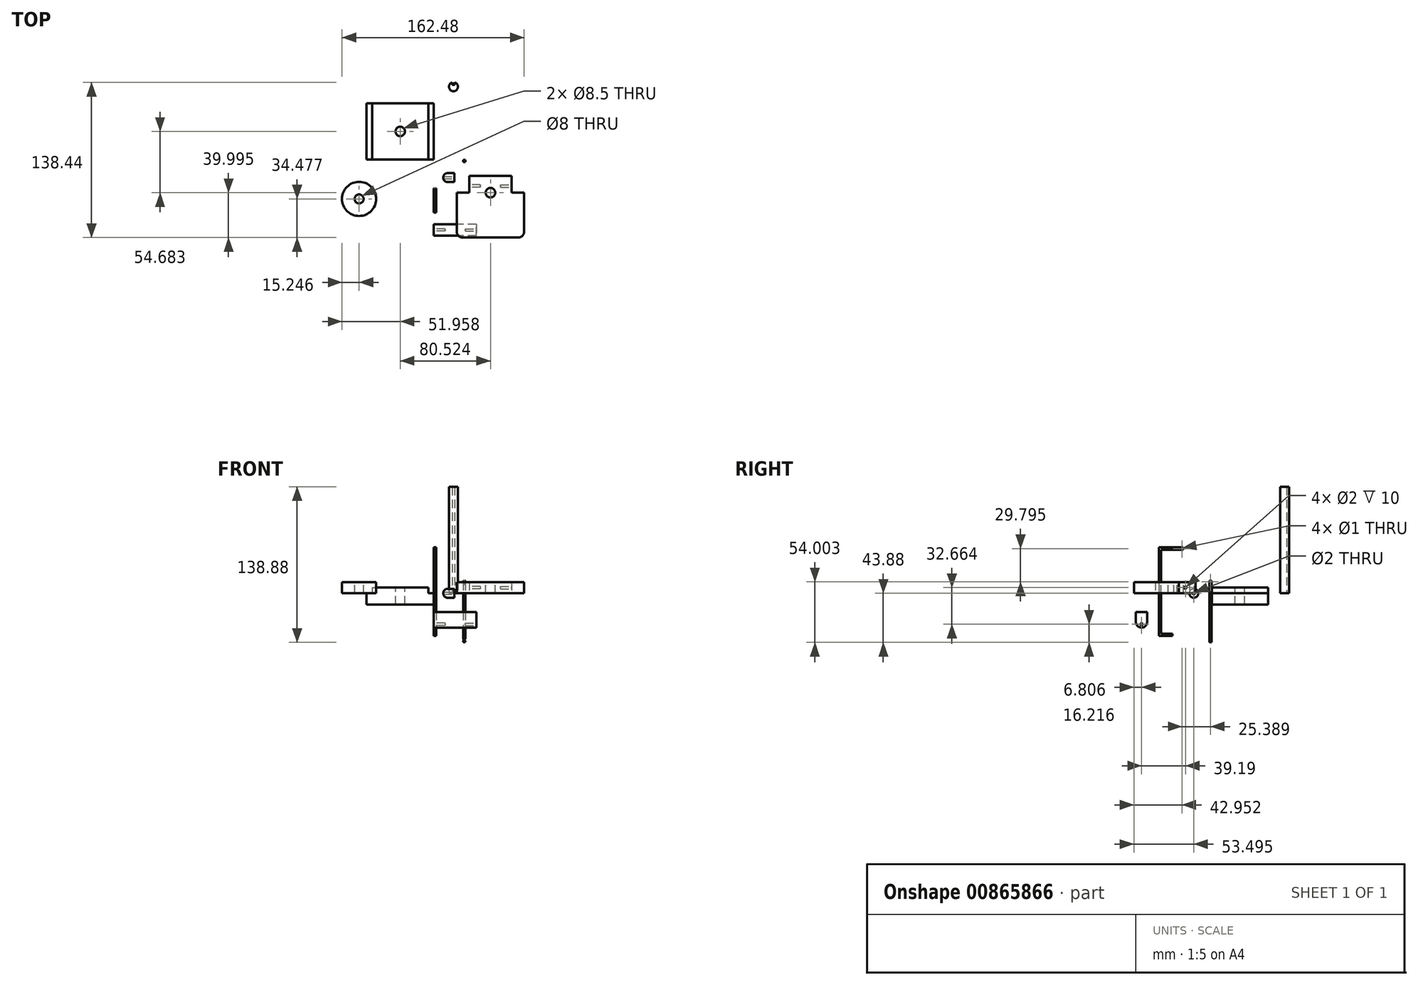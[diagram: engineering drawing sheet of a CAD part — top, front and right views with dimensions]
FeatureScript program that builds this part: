
annotation { "Feature Type Name" : "Feature", "Feature Type Description" : "" }
export const myFeature = defineFeature(function(context is Context, id is Id, definition is map)
    precondition{}
    {
        {
            var Q0;
            Q0=qCreatedBy(makeId("Top.planeOp"),FACE);
            var sketch = newSketch(context, id + "F0", { "sketchPlane" : qUnion([Q0])});
            skLineSegment(sketch, "E0.bottom", {"start": v(-55.02, 50.34) * mm, "end": v(-5.02, 50.34) * mm});
            skLineSegment(sketch, "E0.top", {"start": v(-55.02, 0.34) * mm, "end": v(-5.02, 0.34) * mm});
            skLineSegment(sketch, "E0.left", {"start": v(-55.02, 50.34) * mm, "end": v(-55.02, 0.34) * mm});
            skLineSegment(sketch, "E0.right", {"start": v(-5.02, 50.34) * mm, "end": v(-5.02, 0.34) * mm});
            skSolve(sketch);
        }
        {
            var Q0;
            Q0 = qSketchRegion(id + "F0", true);
            extrude(context, id + "F1", {"entities" : qUnion([Q0]), "depth" : 5 * mm, "offsetDistance" : 25 * mm});
        }
        {
            var Q0;
            Q0=makeQuery(id+"F1.opExtrude","CAP_FACE",FACE,{"disambiguationData":[OSD([sQuery(id+"F0.wireOp",EDGE,"E0.bottom"),sQuery(id+"F0.wireOp",EDGE,"E0.top"),sQuery(id+"F0.wireOp",EDGE,"E0.left"),sQuery(id+"F0.wireOp",EDGE,"E0.right")])],"isStart":true});
            var sketch = newSketch(context, id + "F2", { "sketchPlane" : qUnion([Q0])});
            skLineSegment(sketch, "E1.bottom", {"start": v(-60.02, -0.34) * mm, "end": v(-0.02, -0.34) * mm});
            skLineSegment(sketch, "E1.top", {"start": v(-60.02, -50.34) * mm, "end": v(-0.02, -50.34) * mm});
            skLineSegment(sketch, "E1.left", {"start": v(-60.02, -0.34) * mm, "end": v(-60.02, -50.34) * mm});
            skLineSegment(sketch, "E1.right", {"start": v(-0.02, -0.34) * mm, "end": v(-0.02, -50.34) * mm});
            skSolve(sketch);
        }
        {
            var Q0;
            Q0 = qSketchRegion(id + "F2", true);
            extrude(context, id + "F3", {"entities" : qUnion([Q0]), "operationType" : NewBodyOperationType.ADD, "depth" : 10 * mm, "offsetDistance" : 25 * mm});
        }
        {
            var Q0;
            Q0=makeQuery(id+"F1.opExtrude","CAP_FACE",FACE,{"disambiguationData":[OSD([sQuery(id+"F0.wireOp",EDGE,"E0.bottom"),sQuery(id+"F0.wireOp",EDGE,"E0.top"),sQuery(id+"F0.wireOp",EDGE,"E0.left"),sQuery(id+"F0.wireOp",EDGE,"E0.right")])],"isStart":false});
            var sketch = newSketch(context, id + "F4", { "sketchPlane" : qUnion([Q0])});
            skCircle(sketch, "E2", {"center": v(-30.02, 25.34) * mm, "radius": 4.25 * mm});
            skSolve(sketch);
        }
        {
            var Q0;
            Q0 = qSketchRegion(id + "F4", true);
            extrude(context, id + "F5", {"entities" : qUnion([Q0]), "operationType" : NewBodyOperationType.REMOVE, "endBound" : BoundingType.THROUGH_ALL, "oppositeDirection" : true, "depth" : 25 * mm, "offsetDistance" : 25 * mm});
        }
        {
            var Q0;
            Q0=qCreatedBy(makeId("Top.planeOp"),FACE);
            var sketch = newSketch(context, id + "F6", { "sketchPlane" : qUnion([Q0])});
            skArc(sketch, "E3", {"start": v(16.5, 69.1) * mm, "mid": v(17.5, 61.22) * mm, "end": v(18.5, 69.1) * mm});
            skLineSegment(sketch, "E4", {"start": v(16.5, 69.1) * mm, "end": v(16.5, 67.1) * mm});
            skLineSegment(sketch, "E5", {"start": v(16.5, 67.1) * mm, "end": v(18.5, 67.1) * mm});
            skLineSegment(sketch, "E6", {"start": v(18.5, 67.1) * mm, "end": v(18.5, 69.1) * mm});
            skSolve(sketch);
        }
        {
            var Q0;
            Q0 = qSketchRegion(id + "F6", true);
            extrude(context, id + "F7", {"entities" : qUnion([Q0]), "depth" : 95 * mm, "offsetDistance" : 25 * mm});
        }
        {
            var Q0;
            Q0=qCreatedBy(makeId("Right.planeOp"),FACE);
            var sketch = newSketch(context, id + "F8", { "sketchPlane" : qUnion([Q0])});
            skLineSegment(sketch, "E7", {"start": v(-47.07, -38.08) * mm, "end": v(-35.07, -38.08) * mm});
            skLineSegment(sketch, "E8", {"start": v(-35.07, -38.08) * mm, "end": v(-35.07, -36.08) * mm});
            skLineSegment(sketch, "E9", {"start": v(-35.07, -36.08) * mm, "end": v(-45.07, -36.08) * mm});
            skLineSegment(sketch, "E10", {"start": v(-45.07, -36.08) * mm, "end": v(-45.07, 38.92) * mm});
            skLineSegment(sketch, "E11", {"start": v(-45.07, 38.92) * mm, "end": v(-25.39, 38.92) * mm});
            skLineSegment(sketch, "E12", {"start": v(-25.39, 38.92) * mm, "end": v(-25.39, 40.92) * mm});
            skLineSegment(sketch, "E13", {"start": v(-25.39, 40.92) * mm, "end": v(-47.07, 40.92) * mm});
            skLineSegment(sketch, "E14", {"start": v(-47.07, 40.92) * mm, "end": v(-47.07, -38.08) * mm});
            skSolve(sketch);
        }
        {
            var Q0;
            Q0 = qSketchRegion(id + "F8", true);
            extrude(context, id + "F9", {"entities" : qUnion([Q0]), "depth" : 2 * mm, "offsetDistance" : 25 * mm});
        }
        {
            var Q0;
            Q0=makeQuery(id+"F9.opExtrude","SWEPT_FACE",FACE,{"disambiguationData":[OSD([sQuery(id+"F8.wireOp",EDGE,"E12")])]});
            var sketch = newSketch(context, id + "F10", { "sketchPlane" : qUnion([Q0])});
            skLineSegment(sketch, "E15.bottom", {"start": v(-1.5, 40.92) * mm, "end": v(-0.5, 40.92) * mm});
            skLineSegment(sketch, "E15.top", {"start": v(-1.5, 38.92) * mm, "end": v(-0.5, 38.92) * mm});
            skLineSegment(sketch, "E15.left", {"start": v(-1.5, 40.92) * mm, "end": v(-1.5, 38.92) * mm});
            skLineSegment(sketch, "E15.right", {"start": v(-0.5, 40.92) * mm, "end": v(-0.5, 38.92) * mm});
            skSolve(sketch);
        }
        {
            var Q0;
            Q0 = qSketchRegion(id + "F10", true);
            extrude(context, id + "F11", {"entities" : qUnion([Q0]), "operationType" : NewBodyOperationType.REMOVE, "oppositeDirection" : true, "depth" : 3 * mm, "offsetDistance" : 25 * mm});
        }
        {
            var Q0;
            Q0=makeQuery(id+"F9.opExtrude","CAP_FACE",FACE,{"disambiguationData":[OSD([sQuery(id+"F8.wireOp",EDGE,"E7"),sQuery(id+"F8.wireOp",EDGE,"E8"),sQuery(id+"F8.wireOp",EDGE,"E9"),sQuery(id+"F8.wireOp",EDGE,"E10"),sQuery(id+"F8.wireOp",EDGE,"E11"),sQuery(id+"F8.wireOp",EDGE,"E12"),sQuery(id+"F8.wireOp",EDGE,"E13"),sQuery(id+"F8.wireOp",EDGE,"E14")])],"isStart":false});
            var sketch = newSketch(context, id + "F12", { "sketchPlane" : qUnion([Q0])});
            skCircle(sketch, "E16", {"center": v(-26.39, 39.92) * mm, "radius": 0.5 * mm});
            skPoint(sketch, "E16.centerSnap0", {"position": v(-25.39, 39.92) * mm});
            skSolve(sketch);
        }
        {
            var Q0;
            Q0 = qSketchRegion(id + "F12", true);
            extrude(context, id + "F13", {"entities" : qUnion([Q0]), "operationType" : NewBodyOperationType.REMOVE, "endBound" : BoundingType.THROUGH_ALL, "oppositeDirection" : true, "depth" : 25 * mm, "offsetDistance" : 25 * mm});
        }
        {
            var Q0;
            Q0=qCreatedBy(makeId("Front.planeOp"),FACE);
            var sketch = newSketch(context, id + "F14", { "sketchPlane" : qUnion([Q0])});
            skLineSegment(sketch, "E17.bottom", {"start": v(26.1, 11.12) * mm, "end": v(26.6, 11.12) * mm});
            skLineSegment(sketch, "E17.top", {"start": v(26.6, -43.88) * mm, "end": v(27.6, -43.88) * mm});
            skLineSegment(sketch, "E17.left", {"start": v(26.1, 11.12) * mm, "end": v(26.1, -40.88) * mm});
            skLineSegment(sketch, "E17.right", {"start": v(28.1, 11.12) * mm, "end": v(28.1, -40.88) * mm});
            skLineSegment(sketch, "E18", {"start": v(26.6, 11.12) * mm, "end": v(26.6, 8.12) * mm});
            skLineSegment(sketch, "E19", {"start": v(26.6, 8.12) * mm, "end": v(27.6, 8.12) * mm});
            skLineSegment(sketch, "E20", {"start": v(27.6, 8.12) * mm, "end": v(27.6, 11.12) * mm});
            skLineSegment(sketch, "E21.trimOffspring", {"start": v(27.6, 11.12) * mm, "end": v(28.1, 11.12) * mm});
            skLineSegment(sketch, "E22", {"start": v(26.1, -40.88) * mm, "end": v(26.6, -40.88) * mm});
            skLineSegment(sketch, "E23", {"start": v(26.6, -40.88) * mm, "end": v(26.6, -43.88) * mm});
            skLineSegment(sketch, "E24", {"start": v(28.1, -40.88) * mm, "end": v(27.6, -40.88) * mm});
            skLineSegment(sketch, "E25", {"start": v(27.6, -40.88) * mm, "end": v(27.6, -43.88) * mm});
            skSolve(sketch);
        }
        {
            var Q0;
            Q0 = qSketchRegion(id + "F14", true);
            extrude(context, id + "F15", {"entities" : qUnion([Q0]), "depth" : 2 * mm, "offsetDistance" : 25 * mm});
        }
        {
            var Q0;
            Q0=makeQuery(id+"F15.opExtrude","SWEPT_FACE",FACE,{"disambiguationData":[OSD([sQuery(id+"F14.wireOp",EDGE,"E17.left")])]});
            var sketch = newSketch(context, id + "F16", { "sketchPlane" : qUnion([Q0])});
            skCircle(sketch, "E26", {"center": v(1, 10.12) * mm, "radius": 0.5 * mm});
            skPoint(sketch, "E26.centerSnap0", {"position": v(1, 11.12) * mm});
            skSolve(sketch);
        }
        {
            var Q0;
            Q0 = qSketchRegion(id + "F16", true);
            extrude(context, id + "F17", {"entities" : qUnion([Q0]), "operationType" : NewBodyOperationType.REMOVE, "endBound" : BoundingType.THROUGH_ALL, "oppositeDirection" : true, "depth" : 25 * mm, "offsetDistance" : 25 * mm});
        }
        {
            var Q0;
            Q0=makeQuery(id+"F15.opExtrude","SWEPT_FACE",FACE,{"disambiguationData":[OSD([sQuery(id+"F14.wireOp",EDGE,"E23")])]});
            var sketch = newSketch(context, id + "F18", { "sketchPlane" : qUnion([Q0])});
            skCircle(sketch, "E27", {"center": v(1, -42.88) * mm, "radius": 0.5 * mm});
            skPoint(sketch, "E27.centerSnap0", {"position": v(1, -43.88) * mm});
            skSolve(sketch);
        }
        {
            var Q0;
            Q0 = qSketchRegion(id + "F18", true);
            extrude(context, id + "F19", {"entities" : qUnion([Q0]), "operationType" : NewBodyOperationType.ADD, "depth" : 0.5 * mm, "offsetDistance" : 25 * mm, "hasSecondDirection" : true, "secondDirectionOppositeDirection" : true, "secondDirectionDepth" : 1.5 * mm});
        }
        {
            var Q0;
            Q0=qCreatedBy(makeId("Top.planeOp"),FACE);
            var sketch = newSketch(context, id + "F20", { "sketchPlane" : qUnion([Q0])});
            skCircle(sketch, "E28", {"center": v(-66.73, -34.86) * mm, "radius": 15.25 * mm});
            skLineSegment(sketch, "E29", {"start": v(31.5, -14.34) * mm, "end": v(69.5, -14.34) * mm});
            skLineSegment(sketch, "E30", {"start": v(69.5, -14.34) * mm, "end": v(69.5, -29.34) * mm});
            skLineSegment(sketch, "E31", {"start": v(69.5, -29.34) * mm, "end": v(80.5, -29.34) * mm});
            skLineSegment(sketch, "E32", {"start": v(80.5, -29.34) * mm, "end": v(80.5, -69.34) * mm});
            skLineSegment(sketch, "E33", {"start": v(80.5, -69.34) * mm, "end": v(20.5, -69.34) * mm});
            skLineSegment(sketch, "E34", {"start": v(20.5, -69.34) * mm, "end": v(20.5, -29.34) * mm});
            skLineSegment(sketch, "E35", {"start": v(20.5, -29.34) * mm, "end": v(31.5, -29.34) * mm});
            skLineSegment(sketch, "E36", {"start": v(31.5, -29.34) * mm, "end": v(31.5, -14.34) * mm});
            skSolve(sketch);
        }
        {
            var Q0;
            Q0 = qSketchRegion(id + "F20", true);
            extrude(context, id + "F21", {"entities" : qUnion([Q0]), "depth" : 10 * mm, "offsetDistance" : 25 * mm});
        }
        {
            var Q0;
            Q0=makeQuery(id+"F21.opExtrude","CAP_FACE",FACE,{"disambiguationData":[OSD([sQuery(id+"F20.wireOp",EDGE,"E28")])],"isStart":false});
            var sketch = newSketch(context, id + "F22", { "sketchPlane" : qUnion([Q0])});
            skCircle(sketch, "E37", {"center": v(-66.73, -34.86) * mm, "radius": 4 * mm});
            skSolve(sketch);
        }
        {
            var Q0;
            Q0 = qSketchRegion(id + "F22", true);
            extrude(context, id + "F23", {"entities" : qUnion([Q0]), "operationType" : NewBodyOperationType.REMOVE, "endBound" : BoundingType.THROUGH_ALL, "oppositeDirection" : true, "depth" : 25 * mm, "offsetDistance" : 25 * mm});
        }
        {
            var Q0;
            Q0=makeQuery(id+"F21.opExtrude","CAP_FACE",FACE,{"disambiguationData":[OSD([sQuery(id+"F20.wireOp",EDGE,"E29"),sQuery(id+"F20.wireOp",EDGE,"E30"),sQuery(id+"F20.wireOp",EDGE,"E31"),sQuery(id+"F20.wireOp",EDGE,"E32"),sQuery(id+"F20.wireOp",EDGE,"E33"),sQuery(id+"F20.wireOp",EDGE,"E34"),sQuery(id+"F20.wireOp",EDGE,"E35"),sQuery(id+"F20.wireOp",EDGE,"E36")])],"isStart":false});
            var sketch = newSketch(context, id + "F24", { "sketchPlane" : qUnion([Q0])});
            skCircle(sketch, "E38", {"center": v(50.5, -29.34) * mm, "radius": 4.25 * mm});
            skPoint(sketch, "E38.centerSnap0", {"position": v(50.5, -14.34) * mm});
            skSolve(sketch);
        }
        {
            var Q0;
            Q0 = qSketchRegion(id + "F24", true);
            extrude(context, id + "F25", {"entities" : qUnion([Q0]), "operationType" : NewBodyOperationType.REMOVE, "oppositeDirection" : true, "depth" : 25 * mm, "offsetDistance" : 25 * mm});
        }
        {
            var Q0;
            Q0=makeQuery(id+"F21.opExtrude","SWEPT_FACE",FACE,{"disambiguationData":[OSD([sQuery(id+"F20.wireOp",EDGE,"E30")])]});
            var sketch = newSketch(context, id + "F26", { "sketchPlane" : qUnion([Q0])});
            skCircle(sketch, "E39", {"center": v(-23.34, 5) * mm, "radius": 1 * mm});
            skPoint(sketch, "E39.centerSnap0", {"position": v(-14.34, 5) * mm});
            skSolve(sketch);
        }
        {
            var Q0;
            Q0 = qSketchRegion(id + "F26", true);
            extrude(context, id + "F27", {"entities" : qUnion([Q0]), "operationType" : NewBodyOperationType.REMOVE, "oppositeDirection" : true, "depth" : 10 * mm, "offsetDistance" : 25 * mm});
        }
        {
            var Q0;
            Q0=makeQuery(id+"F21.opExtrude","SWEPT_FACE",FACE,{"disambiguationData":[OSD([sQuery(id+"F20.wireOp",EDGE,"E36")])]});
            var sketch = newSketch(context, id + "F28", { "sketchPlane" : qUnion([Q0])});
            skCircle(sketch, "E40", {"center": v(23.34, 5) * mm, "radius": 1 * mm});
            skPoint(sketch, "E40.centerSnap0", {"position": v(14.34, 5) * mm});
            skSolve(sketch);
        }
        {
            var Q0;
            Q0 = qSketchRegion(id + "F28", true);
            extrude(context, id + "F29", {"entities" : qUnion([Q0]), "operationType" : NewBodyOperationType.REMOVE, "oppositeDirection" : true, "depth" : 10 * mm, "offsetDistance" : 25 * mm});
        }
        {
            var Q0;
            Q0=qCreatedBy(makeId("Right.planeOp"),FACE);
            var sketch = newSketch(context, id + "F30", { "sketchPlane" : qUnion([Q0])});
            skArc(sketch, "E41", {"start": v(-67.53, -25.66) * mm, "mid": v(-62.53, -30.66) * mm, "end": v(-57.53, -25.66) * mm});
            skLineSegment(sketch, "E42", {"start": v(-57.53, -25.66) * mm, "end": v(-57.53, -16.66) * mm});
            skLineSegment(sketch, "E43", {"start": v(-57.53, -16.66) * mm, "end": v(-67.53, -16.66) * mm});
            skLineSegment(sketch, "E44", {"start": v(-67.53, -16.66) * mm, "end": v(-67.53, -25.66) * mm});
            skSolve(sketch);
        }
        {
            var Q0;
            Q0 = qSketchRegion(id + "F30", true);
            extrude(context, id + "F31", {"entities" : qUnion([Q0]), "depth" : 38 * mm, "offsetDistance" : 25 * mm});
        }
        {
            var Q0;
            Q0=makeQuery(id+"F31.opExtrude","CAP_FACE",FACE,{"disambiguationData":[OSD([sQuery(id+"F30.wireOp",EDGE,"E41"),sQuery(id+"F30.wireOp",EDGE,"E42"),sQuery(id+"F30.wireOp",EDGE,"E43"),sQuery(id+"F30.wireOp",EDGE,"E44")])],"isStart":true});
            var sketch = newSketch(context, id + "F32", { "sketchPlane" : qUnion([Q0])});
            skCircle(sketch, "E45", {"center": v(62.53, -27.66) * mm, "radius": 1 * mm});
            skPoint(sketch, "E45.centerSnap0", {"position": v(62.53, -16.66) * mm});
            skSolve(sketch);
        }
        {
            var Q0;
            Q0 = qSketchRegion(id + "F32", true);
            extrude(context, id + "F33", {"entities" : qUnion([Q0]), "operationType" : NewBodyOperationType.REMOVE, "oppositeDirection" : true, "depth" : 10 * mm, "offsetDistance" : 25 * mm});
        }
        {
            var Q0;
            Q0=makeQuery(id+"F31.opExtrude","CAP_FACE",FACE,{"disambiguationData":[OSD([sQuery(id+"F30.wireOp",EDGE,"E41"),sQuery(id+"F30.wireOp",EDGE,"E42"),sQuery(id+"F30.wireOp",EDGE,"E43"),sQuery(id+"F30.wireOp",EDGE,"E44")])],"isStart":false});
            var sketch = newSketch(context, id + "F34", { "sketchPlane" : qUnion([Q0])});
            skCircle(sketch, "E46", {"center": v(-62.53, -27.66) * mm, "radius": 1 * mm});
            skPoint(sketch, "E46.centerSnap0", {"position": v(-62.53, -16.66) * mm});
            skSolve(sketch);
        }
        {
            var Q0;
            Q0 = qSketchRegion(id + "F34", true);
            extrude(context, id + "F35", {"entities" : qUnion([Q0]), "operationType" : NewBodyOperationType.REMOVE, "oppositeDirection" : true, "depth" : 10 * mm, "offsetDistance" : 25 * mm});
        }
        {
            var Q0;
            Q0=makeQuery(id+"F21.opExtrude","SWEPT_EDGE",EDGE,{"disambiguationData":[OSD([sQuery(id+"F20.wireOp",EDGE,"E32"),sQuery(id+"F20.wireOp",EDGE,"E33")])]});
            var Q1;
            Q1=makeQuery(id+"F21.opExtrude","SWEPT_EDGE",EDGE,{"disambiguationData":[OSD([sQuery(id+"F20.wireOp",EDGE,"E33"),sQuery(id+"F20.wireOp",EDGE,"E34")])]});
            fillet(context, id + "F36", {"entities" : qUnion([Q0, Q1]), "tangentPropagation" : true, "radius" : 5 * mm, "defaultsChanged" : false, "vertexSettings" : [], "allowEdgeOverflow" : false});
        }
        {
            var Q0;
            Q0=qCreatedBy(makeId("Top.planeOp"),FACE);
            var sketch = newSketch(context, id + "F37", { "sketchPlane" : qUnion([Q0])});
            skLineSegment(sketch, "E47", {"start": v(8.35, -15.85) * mm, "end": v(18.35, -15.85) * mm});
            skLineSegment(sketch, "E48", {"start": v(18.35, -15.85) * mm, "end": v(18.35, -11.85) * mm});
            skLineSegment(sketch, "E49", {"start": v(18.35, -11.85) * mm, "end": v(12.35, -11.85) * mm});
            skArc(sketch, "E50", {"start": v(12.35, -11.85) * mm, "mid": v(9.53, -13.02) * mm, "end": v(8.35, -15.85) * mm});
            skSolve(sketch);
        }
        {
            var Q0;
            Q0 = qSketchRegion(id + "F37", true);
            var Q1;
            Q1=sQuery(id+"F37.wireOp",EDGE,"E47");
            revolve(context, id + "F38", {"surfaceOperationType" : NewSurfaceOperationType.NEW, "entities" : qUnion([Q0]), "axis" : qUnion([Q1]), "revolveType" : RevolveType.FULL});
        }
        {
            var Q0;
            Q0=makeQuery(id+"F38.opRevolve","SWEPT_FACE",FACE,{"disambiguationData":[OSD([sQuery(id+"F37.wireOp",EDGE,"E48")])]});
            var sketch = newSketch(context, id + "F39", { "sketchPlane" : qUnion([Q0])});
            skCircle(sketch, "E51", {"center": v(-15.85, 0) * mm, "radius": 1 * mm});
            skSolve(sketch);
        }
        {
            var Q0;
            Q0 = qSketchRegion(id + "F39", true);
            extrude(context, id + "F40", {"entities" : qUnion([Q0]), "operationType" : NewBodyOperationType.REMOVE, "oppositeDirection" : true, "depth" : 25 * mm, "offsetDistance" : 25 * mm});
        }
    });
